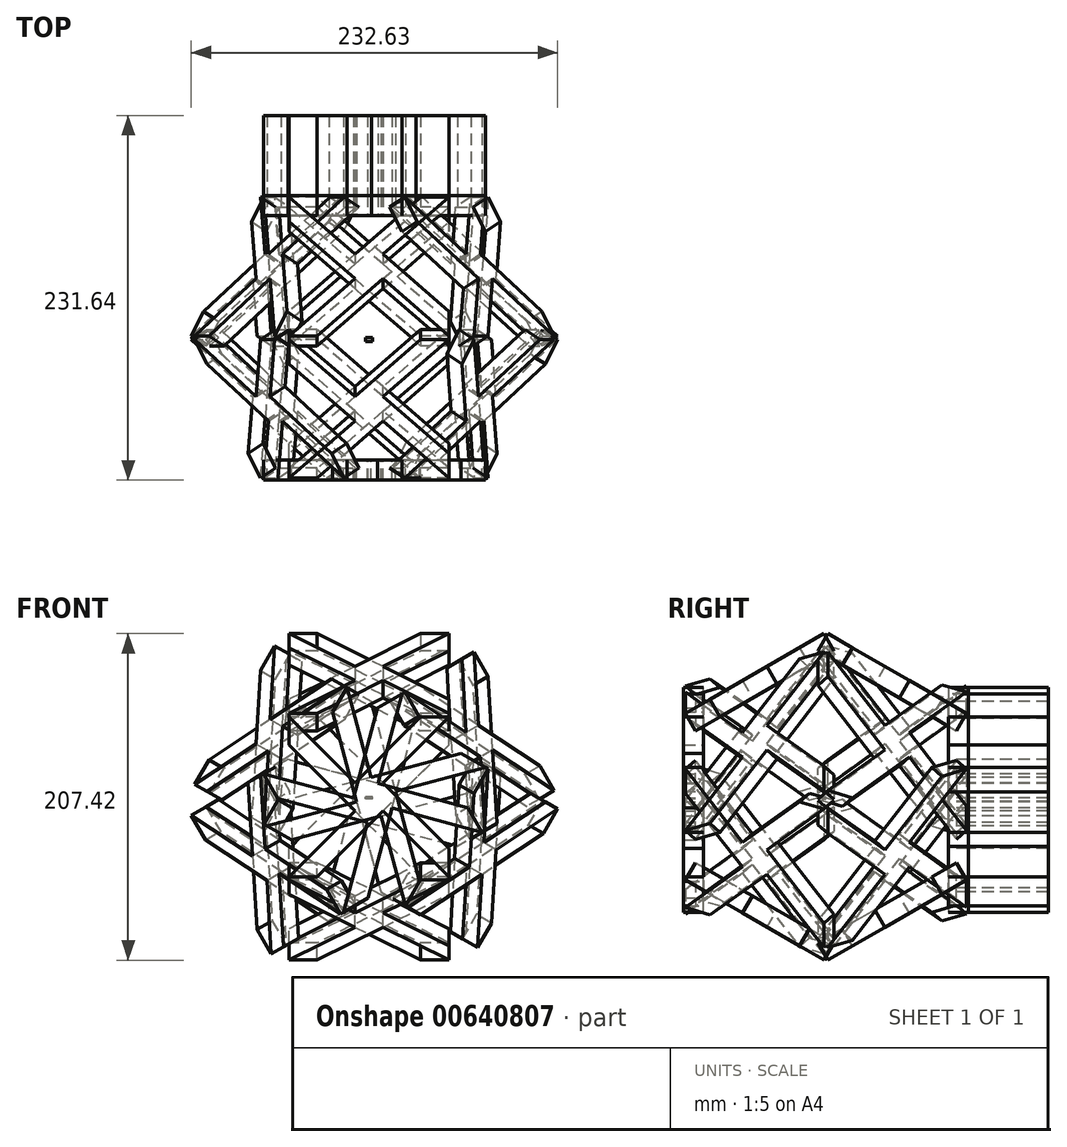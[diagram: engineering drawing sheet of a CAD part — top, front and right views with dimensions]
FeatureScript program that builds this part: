
annotation { "Feature Type Name" : "Feature", "Feature Type Description" : "" }
export const myFeature = defineFeature(function(context is Context, id is Id, definition is map)
    precondition{}
    {
        {
            var Q0;
            Q0=qCreatedBy(makeId("Front.planeOp"),FACE);
            var sketch = newSketch(context, id + "F0", { "sketchPlane" : qUnion([Q0])});
            skLineSegment(sketch, "E0.bottom", {"start": v(50.8, 50.8) * mm, "end": v(-50.8, 50.8) * mm});
            skLineSegment(sketch, "E0.top", {"start": v(50.8, -50.8) * mm, "end": v(-50.8, -50.8) * mm});
            skLineSegment(sketch, "E0.left", {"start": v(50.8, 50.8) * mm, "end": v(50.8, -50.8) * mm});
            skLineSegment(sketch, "E0.right", {"start": v(-50.8, 50.8) * mm, "end": v(-50.8, -50.8) * mm});
            skPoint(sketch, "E0.middle", {"position": v(0, 0) * mm});
            skLineSegment(sketch, "E1", {"start": v(-50.8, 50.8) * mm, "end": v(0, 0) * mm});
            skLineSegment(sketch, "E2", {"start": v(0, 0) * mm, "end": v(-50.8, -50.8) * mm});
            skLineSegment(sketch, "E3", {"start": v(-8.98, -8.98) * mm, "end": v(-50.8, 32.84) * mm});
            skLineSegment(sketch, "E4", {"start": v(-50.8, 32.84) * mm, "end": v(-50.8, -3.08) * mm});
            skLineSegment(sketch, "E5", {"start": v(-50.8, -3.08) * mm, "end": v(-26.94, -26.94) * mm});
            skLineSegment(sketch, "E6", {"start": v(-50.8, 14.88) * mm, "end": v(-17.96, -17.96) * mm});
            skLineSegment(sketch, "E7", {"start": v(-50.8, -21.04) * mm, "end": v(-35.92, -35.92) * mm});
            skLineSegment(sketch, "E8", {"start": v(-44.9, -44.9) * mm, "end": v(-50.8, -39) * mm});
            skLineSegment(sketch, "E9.1.1", {"start": v(-50.8, -50.8) * mm, "end": v(0, 0) * mm});
            skLineSegment(sketch, "E9.1.2", {"start": v(8.98, -8.98) * mm, "end": v(-32.84, -50.8) * mm});
            skLineSegment(sketch, "E9.1.3", {"start": v(-14.88, -50.8) * mm, "end": v(17.96, -17.96) * mm});
            skLineSegment(sketch, "E9.1.4", {"start": v(3.08, -50.8) * mm, "end": v(26.94, -26.94) * mm});
            skLineSegment(sketch, "E9.1.5", {"start": v(21.04, -50.8) * mm, "end": v(35.92, -35.92) * mm});
            skLineSegment(sketch, "E9.1.6", {"start": v(44.9, -44.9) * mm, "end": v(39, -50.8) * mm});
            skLineSegment(sketch, "E9.2.1", {"start": v(50.8, -50.8) * mm, "end": v(0, 0) * mm});
            skLineSegment(sketch, "E9.2.2", {"start": v(8.98, 8.98) * mm, "end": v(50.8, -32.84) * mm});
            skLineSegment(sketch, "E9.2.3", {"start": v(50.8, -14.88) * mm, "end": v(17.96, 17.96) * mm});
            skLineSegment(sketch, "E9.2.4", {"start": v(50.8, 3.08) * mm, "end": v(26.94, 26.94) * mm});
            skLineSegment(sketch, "E9.2.5", {"start": v(50.8, 21.04) * mm, "end": v(35.92, 35.92) * mm});
            skLineSegment(sketch, "E9.2.6", {"start": v(44.9, 44.9) * mm, "end": v(50.8, 39) * mm});
            skLineSegment(sketch, "E9.3.1", {"start": v(50.8, 50.8) * mm, "end": v(0, 0) * mm});
            skLineSegment(sketch, "E9.3.2", {"start": v(-8.98, 8.98) * mm, "end": v(32.84, 50.8) * mm});
            skLineSegment(sketch, "E9.3.3", {"start": v(14.88, 50.8) * mm, "end": v(-17.96, 17.96) * mm});
            skLineSegment(sketch, "E9.3.4", {"start": v(-3.08, 50.8) * mm, "end": v(-26.94, 26.94) * mm});
            skLineSegment(sketch, "E9.3.5", {"start": v(-21.04, 50.8) * mm, "end": v(-35.92, 35.92) * mm});
            skLineSegment(sketch, "E9.3.6", {"start": v(-44.9, 44.9) * mm, "end": v(-39, 50.8) * mm});
            skSolve(sketch);
        }
        {
            var Q0;
            {var subQ7=sQuery(id+"F0.wireOp",EDGE,"E9.3.2");Q0=makeQuery(id+"F0.imprint","IMPRINT",FACE,{"disambiguationData":[TD([[makeQuery(id+"F0.imprint","IMPRINT",EDGE,{"derivedFrom":subQ7}),-1.0]])]});}
            var Q1;
            {var subQ5=sQuery(id+"F0.wireOp",EDGE,"E3");Q1=makeQuery(id+"F0.imprint","IMPRINT",FACE,{"disambiguationData":[TD([[makeQuery(id+"F0.imprint","IMPRINT",EDGE,{"derivedFrom":subQ5}),-1.0]])]});}
            var Q2;
            {var subQ6=sQuery(id+"F0.wireOp",EDGE,"E9.1.2");Q2=makeQuery(id+"F0.imprint","IMPRINT",FACE,{"disambiguationData":[TD([[makeQuery(id+"F0.imprint","IMPRINT",EDGE,{"derivedFrom":subQ6}),-1.0]])]});}
            var Q3;
            {var subQ6=sQuery(id+"F0.wireOp",EDGE,"E9.2.2");Q3=makeQuery(id+"F0.imprint","IMPRINT",FACE,{"disambiguationData":[TD([[makeQuery(id+"F0.imprint","IMPRINT",EDGE,{"derivedFrom":subQ6}),-1.0]])]});}
            extrude(context, id + "F1", {"entities" : qUnion([Q0, Q1, Q2, Q3]), "depth" : 12.7 * mm, "offsetDistance" : 25.4 * mm});
        }
        {
            var Q0;
            Q0=qCreatedBy(makeId("Top.planeOp"),FACE);
            var sketch = newSketch(context, id + "F2", { "sketchPlane" : qUnion([Q0])});
            skLineSegment(sketch, "E10.bottom", {"start": v(2.3, 75.28) * mm, "end": v(-2.3, 75.28) * mm});
            skLineSegment(sketch, "E10.top", {"start": v(2.3, 77.72) * mm, "end": v(-2.3, 77.72) * mm});
            skLineSegment(sketch, "E10.left", {"start": v(2.3, 75.28) * mm, "end": v(2.3, 77.72) * mm});
            skLineSegment(sketch, "E10.right", {"start": v(-2.3, 75.28) * mm, "end": v(-2.3, 77.72) * mm});
            skPoint(sketch, "E10.middle", {"position": v(0, 76.5) * mm});
            skSolve(sketch);
        }
        {
            var Q0;
            Q0=makeQuery(id+"F2.imprint","IMPRINT",FACE,{"disambiguationData":[TD([[makeQuery(id+"F2.imprint","IMPRINT",EDGE,{"derivedFrom":sQuery(id+"F2.wireOp",EDGE,"E10.bottom")}),-1.0]])]});
            extrude(context, id + "F3", {"entities" : qUnion([Q0]), "oppositeDirection" : true, "depth" : 1.27 * mm, "offsetDistance" : 25.4 * mm});
        }
        {
            var Q0;
            Q0=makeQuery(id+"F1.opExtrude","SWEPT_BODY",BODY,{"disambiguationData":[OSD([sQuery(id+"F0.wireOp",EDGE,"E0.bottom"),sQuery(id+"F0.wireOp",EDGE,"E0.top"),sQuery(id+"F0.wireOp",EDGE,"E0.left"),sQuery(id+"F0.wireOp",EDGE,"E0.right"),sQuery(id+"F0.wireOp",EDGE,"E3"),sQuery(id+"F0.wireOp",EDGE,"E1"),sQuery(id+"F0.wireOp",EDGE,"E9.1.1"),sQuery(id+"F0.wireOp",EDGE,"E9.1.2"),sQuery(id+"F0.wireOp",EDGE,"E9.2.1"),sQuery(id+"F0.wireOp",EDGE,"E9.2.2"),sQuery(id+"F0.wireOp",EDGE,"E9.3.1"),sQuery(id+"F0.wireOp",EDGE,"E9.3.2")])]});
            var Q1;
            Q1=makeQuery(id+"F3.opExtrude","CAP_EDGE",EDGE,{"disambiguationData":[OSD([sQuery(id+"F2.wireOp",EDGE,"E10.top")])],"isStart":true});
            circularPattern(context, id + "F4", {"entities" : qUnion([Q0]), "axis" : qUnion([Q1]), "angle" : 360 * degree, "instanceCount" : 6, "oppositeDirection" : true, "equalSpace" : true});
        }
        {
            var Q0;
            Q0=makeQuery(id+"F4.opPattern","COPY",BODY,{"derivedFrom":makeQuery(id+"F1.opExtrude","SWEPT_BODY",BODY,{"disambiguationData":[OSD([sQuery(id+"F0.wireOp",EDGE,"E0.bottom"),sQuery(id+"F0.wireOp",EDGE,"E0.top"),sQuery(id+"F0.wireOp",EDGE,"E0.left"),sQuery(id+"F0.wireOp",EDGE,"E0.right"),sQuery(id+"F0.wireOp",EDGE,"E3"),sQuery(id+"F0.wireOp",EDGE,"E1"),sQuery(id+"F0.wireOp",EDGE,"E9.1.1"),sQuery(id+"F0.wireOp",EDGE,"E9.1.2"),sQuery(id+"F0.wireOp",EDGE,"E9.2.1"),sQuery(id+"F0.wireOp",EDGE,"E9.2.2"),sQuery(id+"F0.wireOp",EDGE,"E9.3.1"),sQuery(id+"F0.wireOp",EDGE,"E9.3.2")])]}),"instanceName":"5"});
            var Q1;
            Q1=makeQuery(id+"F4.opPattern","COPY",BODY,{"derivedFrom":makeQuery(id+"F1.opExtrude","SWEPT_BODY",BODY,{"disambiguationData":[OSD([sQuery(id+"F0.wireOp",EDGE,"E0.bottom"),sQuery(id+"F0.wireOp",EDGE,"E0.top"),sQuery(id+"F0.wireOp",EDGE,"E0.left"),sQuery(id+"F0.wireOp",EDGE,"E0.right"),sQuery(id+"F0.wireOp",EDGE,"E3"),sQuery(id+"F0.wireOp",EDGE,"E1"),sQuery(id+"F0.wireOp",EDGE,"E9.1.1"),sQuery(id+"F0.wireOp",EDGE,"E9.1.2"),sQuery(id+"F0.wireOp",EDGE,"E9.2.1"),sQuery(id+"F0.wireOp",EDGE,"E9.2.2"),sQuery(id+"F0.wireOp",EDGE,"E9.3.1"),sQuery(id+"F0.wireOp",EDGE,"E9.3.2")])]}),"instanceName":"4"});
            var Q2;
            Q2=makeQuery(id+"F4.opPattern","COPY",BODY,{"derivedFrom":makeQuery(id+"F1.opExtrude","SWEPT_BODY",BODY,{"disambiguationData":[OSD([sQuery(id+"F0.wireOp",EDGE,"E0.bottom"),sQuery(id+"F0.wireOp",EDGE,"E0.top"),sQuery(id+"F0.wireOp",EDGE,"E0.left"),sQuery(id+"F0.wireOp",EDGE,"E0.right"),sQuery(id+"F0.wireOp",EDGE,"E3"),sQuery(id+"F0.wireOp",EDGE,"E1"),sQuery(id+"F0.wireOp",EDGE,"E9.1.1"),sQuery(id+"F0.wireOp",EDGE,"E9.1.2"),sQuery(id+"F0.wireOp",EDGE,"E9.2.1"),sQuery(id+"F0.wireOp",EDGE,"E9.2.2"),sQuery(id+"F0.wireOp",EDGE,"E9.3.1"),sQuery(id+"F0.wireOp",EDGE,"E9.3.2")])]}),"instanceName":"3"});
            var Q3;
            Q3=makeQuery(id+"F4.opPattern","COPY",BODY,{"derivedFrom":makeQuery(id+"F1.opExtrude","SWEPT_BODY",BODY,{"disambiguationData":[OSD([sQuery(id+"F0.wireOp",EDGE,"E0.bottom"),sQuery(id+"F0.wireOp",EDGE,"E0.top"),sQuery(id+"F0.wireOp",EDGE,"E0.left"),sQuery(id+"F0.wireOp",EDGE,"E0.right"),sQuery(id+"F0.wireOp",EDGE,"E3"),sQuery(id+"F0.wireOp",EDGE,"E1"),sQuery(id+"F0.wireOp",EDGE,"E9.1.1"),sQuery(id+"F0.wireOp",EDGE,"E9.1.2"),sQuery(id+"F0.wireOp",EDGE,"E9.2.1"),sQuery(id+"F0.wireOp",EDGE,"E9.2.2"),sQuery(id+"F0.wireOp",EDGE,"E9.3.1"),sQuery(id+"F0.wireOp",EDGE,"E9.3.2")])]}),"instanceName":"2"});
            var Q4;
            Q4=makeQuery(id+"F4.opPattern","COPY",BODY,{"derivedFrom":makeQuery(id+"F1.opExtrude","SWEPT_BODY",BODY,{"disambiguationData":[OSD([sQuery(id+"F0.wireOp",EDGE,"E0.bottom"),sQuery(id+"F0.wireOp",EDGE,"E0.top"),sQuery(id+"F0.wireOp",EDGE,"E0.left"),sQuery(id+"F0.wireOp",EDGE,"E0.right"),sQuery(id+"F0.wireOp",EDGE,"E3"),sQuery(id+"F0.wireOp",EDGE,"E1"),sQuery(id+"F0.wireOp",EDGE,"E9.1.1"),sQuery(id+"F0.wireOp",EDGE,"E9.1.2"),sQuery(id+"F0.wireOp",EDGE,"E9.2.1"),sQuery(id+"F0.wireOp",EDGE,"E9.2.2"),sQuery(id+"F0.wireOp",EDGE,"E9.3.1"),sQuery(id+"F0.wireOp",EDGE,"E9.3.2")])]}),"instanceName":"1"});
            var Q5;
            Q5=makeQuery(id+"F1.opExtrude","SWEPT_BODY",BODY,{"disambiguationData":[OSD([sQuery(id+"F0.wireOp",EDGE,"E0.bottom"),sQuery(id+"F0.wireOp",EDGE,"E0.top"),sQuery(id+"F0.wireOp",EDGE,"E0.left"),sQuery(id+"F0.wireOp",EDGE,"E0.right"),sQuery(id+"F0.wireOp",EDGE,"E3"),sQuery(id+"F0.wireOp",EDGE,"E1"),sQuery(id+"F0.wireOp",EDGE,"E9.1.1"),sQuery(id+"F0.wireOp",EDGE,"E9.1.2"),sQuery(id+"F0.wireOp",EDGE,"E9.2.1"),sQuery(id+"F0.wireOp",EDGE,"E9.2.2"),sQuery(id+"F0.wireOp",EDGE,"E9.3.1"),sQuery(id+"F0.wireOp",EDGE,"E9.3.2")])]});
            var Q6;
            Q6=makeQuery(id+"F3.opExtrude","CAP_EDGE",EDGE,{"disambiguationData":[OSD([sQuery(id+"F2.wireOp",EDGE,"E10.left")])],"isStart":false});
            circularPattern(context, id + "F5", {"entities" : qUnion([Q0, Q1, Q2, Q3, Q4, Q5]), "axis" : qUnion([Q6]), "angle" : 360 * degree, "instanceCount" : 3, "equalSpace" : true});
        }
        {
            var Q0;
            Q0=makeQuery(id+"F4.opPattern","COPY",FACE,{"derivedFrom":makeQuery(id+"F1.opExtrude","CAP_FACE",FACE,{"disambiguationData":[OSD([sQuery(id+"F0.wireOp",EDGE,"E0.bottom"),sQuery(id+"F0.wireOp",EDGE,"E0.top"),sQuery(id+"F0.wireOp",EDGE,"E0.left"),sQuery(id+"F0.wireOp",EDGE,"E0.right"),sQuery(id+"F0.wireOp",EDGE,"E3"),sQuery(id+"F0.wireOp",EDGE,"E1"),sQuery(id+"F0.wireOp",EDGE,"E9.1.1"),sQuery(id+"F0.wireOp",EDGE,"E9.1.2"),sQuery(id+"F0.wireOp",EDGE,"E9.2.1"),sQuery(id+"F0.wireOp",EDGE,"E9.2.2"),sQuery(id+"F0.wireOp",EDGE,"E9.3.1"),sQuery(id+"F0.wireOp",EDGE,"E9.3.2")])],"isStart":false}),"instanceName":"3"});
            var Q1;
            Q1=makeQuery(id+"F5.opPattern","COPY",FACE,{"derivedFrom":makeQuery(id+"F4.opPattern","COPY",FACE,{"derivedFrom":makeQuery(id+"F1.opExtrude","CAP_FACE",FACE,{"disambiguationData":[OSD([sQuery(id+"F0.wireOp",EDGE,"E0.bottom"),sQuery(id+"F0.wireOp",EDGE,"E0.top"),sQuery(id+"F0.wireOp",EDGE,"E0.left"),sQuery(id+"F0.wireOp",EDGE,"E0.right"),sQuery(id+"F0.wireOp",EDGE,"E3"),sQuery(id+"F0.wireOp",EDGE,"E1"),sQuery(id+"F0.wireOp",EDGE,"E9.1.1"),sQuery(id+"F0.wireOp",EDGE,"E9.1.2"),sQuery(id+"F0.wireOp",EDGE,"E9.2.1"),sQuery(id+"F0.wireOp",EDGE,"E9.2.2"),sQuery(id+"F0.wireOp",EDGE,"E9.3.1"),sQuery(id+"F0.wireOp",EDGE,"E9.3.2")])],"isStart":false}),"instanceName":"3"}),"instanceName":"1"});
            var Q2;
            Q2=makeQuery(id+"F5.opPattern","COPY",FACE,{"derivedFrom":makeQuery(id+"F4.opPattern","COPY",FACE,{"derivedFrom":makeQuery(id+"F1.opExtrude","CAP_FACE",FACE,{"disambiguationData":[OSD([sQuery(id+"F0.wireOp",EDGE,"E0.bottom"),sQuery(id+"F0.wireOp",EDGE,"E0.top"),sQuery(id+"F0.wireOp",EDGE,"E0.left"),sQuery(id+"F0.wireOp",EDGE,"E0.right"),sQuery(id+"F0.wireOp",EDGE,"E3"),sQuery(id+"F0.wireOp",EDGE,"E1"),sQuery(id+"F0.wireOp",EDGE,"E9.1.1"),sQuery(id+"F0.wireOp",EDGE,"E9.1.2"),sQuery(id+"F0.wireOp",EDGE,"E9.2.1"),sQuery(id+"F0.wireOp",EDGE,"E9.2.2"),sQuery(id+"F0.wireOp",EDGE,"E9.3.1"),sQuery(id+"F0.wireOp",EDGE,"E9.3.2")])],"isStart":false}),"instanceName":"3"}),"instanceName":"2"});
            extrude(context, id + "F6", {"entities" : qUnion([Q0, Q1, Q2]), "depth" : 50.8 * mm, "offsetDistance" : 25.4 * mm});
        }
    });
